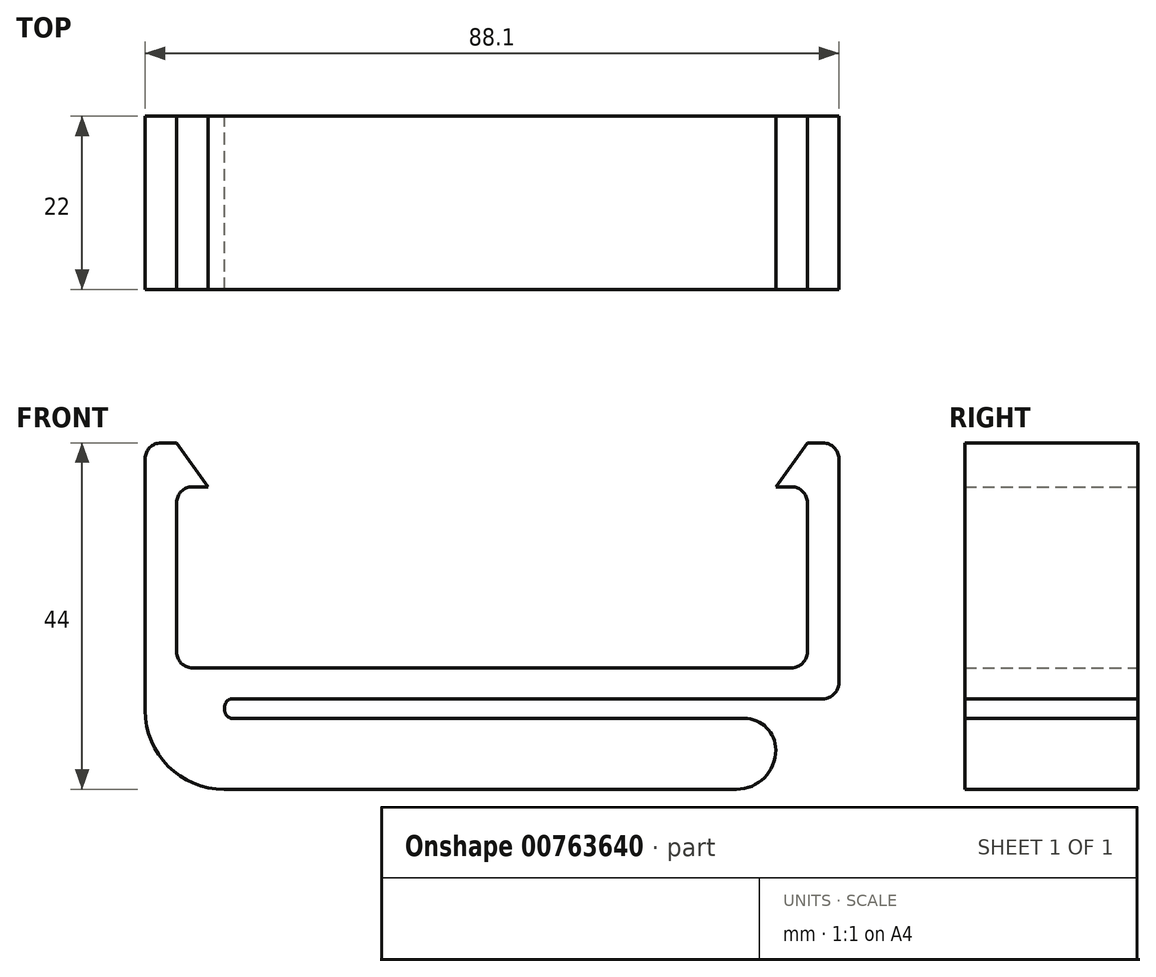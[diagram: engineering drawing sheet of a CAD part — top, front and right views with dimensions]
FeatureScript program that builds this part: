
annotation { "Feature Type Name" : "Feature", "Feature Type Description" : "" }
export const myFeature = defineFeature(function(context is Context, id is Id, definition is map)
    precondition{}
    {
        {
            var Q0;
            Q0=qCreatedBy(makeId("Front.planeOp"),FACE);
            var sketch = newSketch(context, id + "F0", { "sketchPlane" : qUnion([Q0])});
            skLineSegment(sketch, "E0", {"start": v(-80.1, -15.13) * mm, "end": v(-80.1, 10.87) * mm});
            skLineSegment(sketch, "E1", {"start": v(-78.1, 12.87) * mm, "end": v(-76.1, 12.87) * mm});
            skLineSegment(sketch, "E2", {"start": v(-76.1, 12.87) * mm, "end": v(-72.1, 7.3) * mm});
            skLineSegment(sketch, "E3", {"start": v(-72.1, 7.3) * mm, "end": v(-74.1, 7.3) * mm});
            skLineSegment(sketch, "E4", {"start": v(-76.1, 5.3) * mm, "end": v(-76.1, -13.7) * mm});
            skLineSegment(sketch, "E5", {"start": v(-74.1, -15.7) * mm, "end": v(2, -15.7) * mm});
            skLineSegment(sketch, "E6", {"start": v(4, -13.7) * mm, "end": v(4, 5.3) * mm});
            skLineSegment(sketch, "E7", {"start": v(2, 7.3) * mm, "end": v(0, 7.3) * mm});
            skLineSegment(sketch, "E8", {"start": v(0, 7.3) * mm, "end": v(4, 12.87) * mm});
            skLineSegment(sketch, "E9", {"start": v(4, 12.87) * mm, "end": v(6, 12.87) * mm});
            skLineSegment(sketch, "E10", {"start": v(8, 10.87) * mm, "end": v(8, -17.63) * mm});
            skLineSegment(sketch, "E11", {"start": v(6, -19.63) * mm, "end": v(-69, -19.63) * mm});
            skLineSegment(sketch, "E12", {"start": v(-70, -20.63) * mm, "end": v(-70, -21.13) * mm});
            skLineSegment(sketch, "E13", {"start": v(-69, -22.13) * mm, "end": v(-4, -22.13) * mm});
            skLineSegment(sketch, "E14", {"start": v(0, -26.13) * mm, "end": v(0, -26.13) * mm});
            skLineSegment(sketch, "E15", {"start": v(0, -26.13) * mm, "end": v(-75.1, -26.13) * mm});
            skLineSegment(sketch, "E16", {"start": v(-80.1, -21.13) * mm, "end": v(-80.1, -15.13) * mm});
            skPoint(sketch, "E17.visualSharp", {"position": v(-80.1, -26.13) * mm});
            skArc(sketch, "E17.filletArc", {"start": v(-80.1, -21.13) * mm, "mid": v(-78.64, -24.67) * mm, "end": v(-75.1, -26.13) * mm});
            skPoint(sketch, "E18.visualSharp", {"position": v(-80.1, 12.87) * mm});
            skArc(sketch, "E18.filletArc", {"start": v(-78.1, 12.87) * mm, "mid": v(-79.51, 12.28) * mm, "end": v(-80.1, 10.87) * mm});
            skPoint(sketch, "E19.visualSharp", {"position": v(8, 12.87) * mm});
            skArc(sketch, "E19.filletArc", {"start": v(8, 10.87) * mm, "mid": v(7.41, 12.28) * mm, "end": v(6, 12.87) * mm});
            skPoint(sketch, "E20.visualSharp", {"position": v(8, -19.63) * mm});
            skArc(sketch, "E20.filletArc", {"start": v(6, -19.63) * mm, "mid": v(7.41, -19.05) * mm, "end": v(8, -17.63) * mm});
            skPoint(sketch, "E21.visualSharp", {"position": v(4, -15.7) * mm});
            skArc(sketch, "E21.filletArc", {"start": v(2, -15.7) * mm, "mid": v(3.41, -15.11) * mm, "end": v(4, -13.7) * mm});
            skPoint(sketch, "E22.visualSharp", {"position": v(-76.1, -15.7) * mm});
            skArc(sketch, "E22.filletArc", {"start": v(-76.1, -13.7) * mm, "mid": v(-75.51, -15.11) * mm, "end": v(-74.1, -15.7) * mm});
            skPoint(sketch, "E23.visualSharp", {"position": v(4, 7.3) * mm});
            skArc(sketch, "E23.filletArc", {"start": v(4, 5.3) * mm, "mid": v(3.41, 6.71) * mm, "end": v(2, 7.3) * mm});
            skPoint(sketch, "E24.visualSharp", {"position": v(-76.1, 7.3) * mm});
            skArc(sketch, "E24.filletArc", {"start": v(-74.1, 7.3) * mm, "mid": v(-75.51, 6.71) * mm, "end": v(-76.1, 5.3) * mm});
            skPoint(sketch, "E25.visualSharp", {"position": v(0, -22.13) * mm});
            skArc(sketch, "E25.filletArc", {"start": v(0, -26.13) * mm, "mid": v(-1.17, -23.3) * mm, "end": v(-4, -22.13) * mm});
            skPoint(sketch, "E26.visualSharp", {"position": v(-70, -19.63) * mm});
            skArc(sketch, "E26.filletArc", {"start": v(-69, -19.63) * mm, "mid": v(-69.7, -19.93) * mm, "end": v(-70, -20.63) * mm});
            skPoint(sketch, "E27.visualSharp", {"position": v(-70, -22.13) * mm});
            skArc(sketch, "E27.filletArc", {"start": v(-70, -21.13) * mm, "mid": v(-69.7, -21.84) * mm, "end": v(-69, -22.13) * mm});
            skSolve(sketch);
        }
        {
            var Q0;
            Q0=makeQuery(id+"F0.imprint","IMPRINT",FACE,{"disambiguationData":[TD([[makeQuery(id+"F0.imprint","IMPRINT",EDGE,{"derivedFrom":sQuery(id+"F0.wireOp",EDGE,"E0")}),-1.0]])]});
            extrude(context, id + "F1", {"entities" : qUnion([Q0]), "depth" : 22 * mm, "offsetDistance" : 25 * mm});
        }
        {
            var Q0;
            Q0=makeQuery(id+"F1.opExtrude","SWEPT_FACE",FACE,{"disambiguationData":[OSD([sQuery(id+"F0.wireOp",EDGE,"E15")])]});
            var Q1;
            Q1=makeQuery(id+"F1.opExtrude","SWEPT_FACE",FACE,{"disambiguationData":[OSD([sQuery(id+"F0.wireOp",EDGE,"E17.filletArc")])]});
            extrude(context, id + "F2", {"entities" : qUnion([Q0]), "operationType" : NewBodyOperationType.ADD, "depth" : 5 * mm, "endBoundEntityFace" : qUnion([Q1]), "offsetDistance" : 25 * mm});
        }
        {
            var Q0;
            Q0=makeQuery(id+"F2.opExtrude","SWEPT_FACE",FACE,{"disambiguationData":[OSD([sQuery(id+"F0.wireOp",EDGE,"E15"),sQuery(id+"F0.wireOp",EDGE,"E17.filletArc")])]});
            var Q1;
            Q1=makeQuery(id+"F1.opExtrude","SWEPT_FACE",FACE,{"disambiguationData":[OSD([sQuery(id+"F0.wireOp",EDGE,"E0"),sQuery(id+"F0.wireOp",EDGE,"E16")])]});
            extrude(context, id + "F3", {"entities" : qUnion([Q0]), "operationType" : NewBodyOperationType.ADD, "endBound" : BoundingType.UP_TO_SURFACE, "depth" : 25 * mm, "endBoundEntityFace" : qUnion([Q1]), "offsetDistance" : 25 * mm});
        }
        {
            var Q0;
            {var subQ0=sQuery(id+"F0.wireOp",EDGE,"E17.filletArc");var subQ1=sQuery(id+"F0.wireOp",EDGE,"E15");Q0=makeQuery(id+"F3.opExtrude","SWEPT_FACE",FACE,{"disambiguationData":[OSD([subQ1,subQ0]),TDD([makeQuery(id+"F2.boolean.opBoolean","MERGE",EDGE,{"derivedFrom":[makeQuery(id+"F1.opExtrude","SWEPT_EDGE",EDGE,{"disambiguationData":[OSD([subQ1,subQ0])]}),makeQuery(id+"F2.opExtrude","CAP_EDGE",EDGE,{"disambiguationData":[OSD([subQ1,subQ0])],"isStart":true})]})])]});}
            extrude(context, id + "F4", {"entities" : qUnion([Q0]), "operationType" : NewBodyOperationType.ADD, "depth" : 5 * mm, "offsetDistance" : 25 * mm});
        }
        {
            var Q0;
            {var subQ0=sQuery(id+"F0.wireOp",EDGE,"E17.filletArc");var subQ1=sQuery(id+"F0.wireOp",EDGE,"E15");Q0=makeQuery(id+"F3.opExtrude","CAP_EDGE",EDGE,{"disambiguationData":[OSD([subQ1,subQ0]),TDD([makeQuery(id+"F2.opExtrude","CAP_EDGE",EDGE,{"disambiguationData":[OSD([subQ1,subQ0])],"isStart":false})])],"isStart":false});}
            fillet(context, id + "F5", {"entities" : qUnion([Q0]), "radius" : 10 * mm, "tangentPropagation" : true, "allowEdgeOverflow" : false});
        }
        {
            var Q0;
            Q0=makeQuery(id+"F2.opExtrude","CAP_EDGE",EDGE,{"disambiguationData":[OSD([sQuery(id+"F0.wireOp",EDGE,"E15"),sQuery(id+"F0.wireOp",EDGE,"E25.filletArc")])],"isStart":false});
            fillet(context, id + "F6", {"entities" : qUnion([Q0]), "radius" : 5 * mm, "tangentPropagation" : true, "allowEdgeOverflow" : false});
        }
    });
